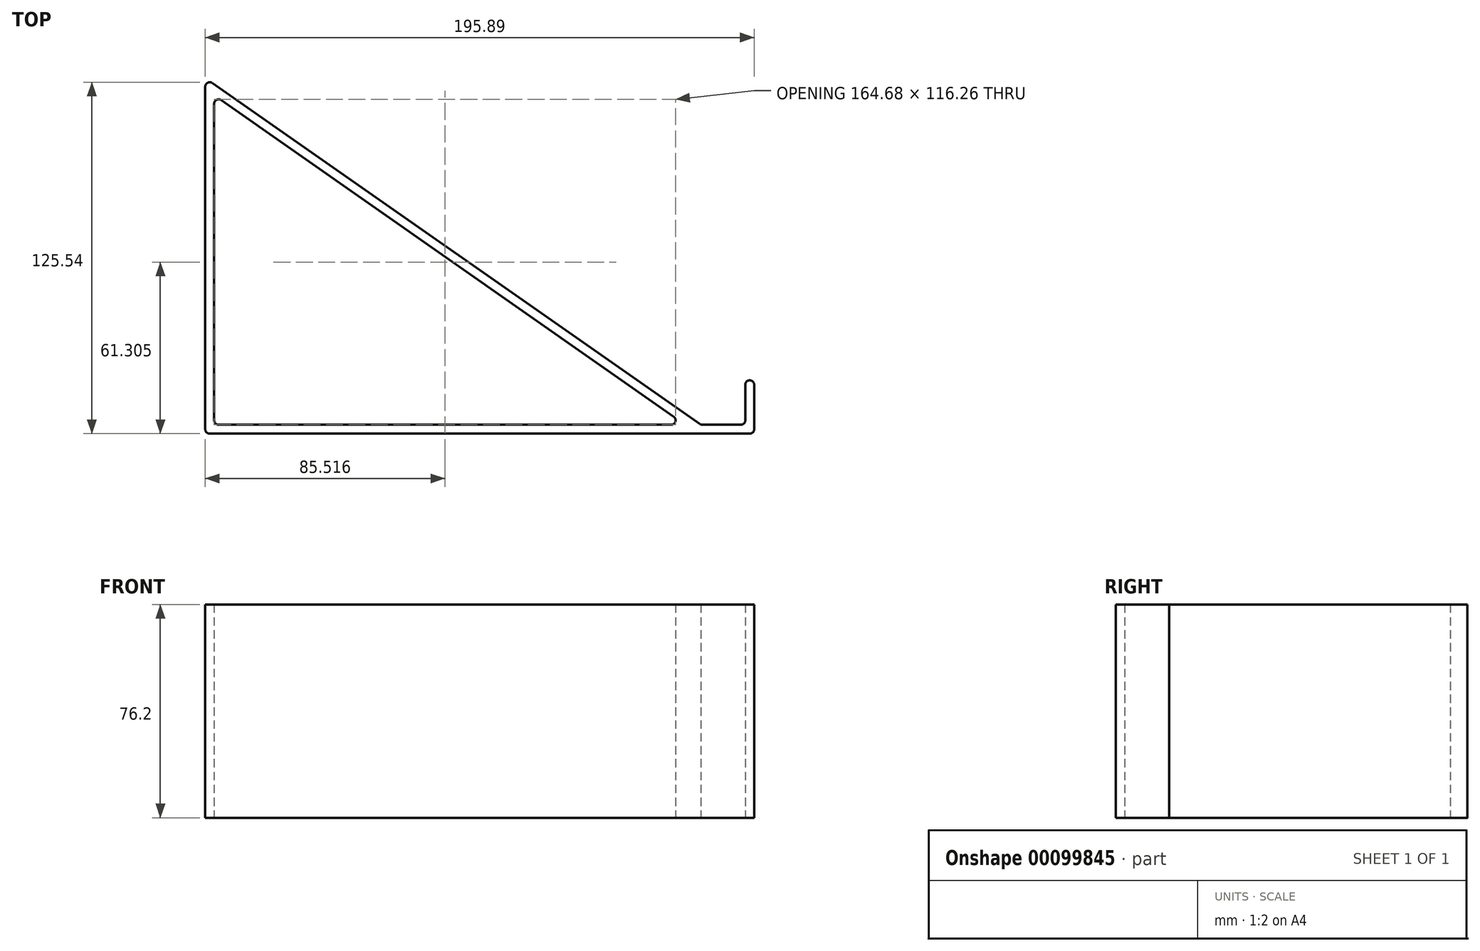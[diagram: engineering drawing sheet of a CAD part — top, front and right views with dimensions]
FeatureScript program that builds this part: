
annotation { "Feature Type Name" : "Feature", "Feature Type Description" : "" }
export const myFeature = defineFeature(function(context is Context, id is Id, definition is map)
    precondition{}
    {
        {
            var Q0;
            Q0=qCreatedBy(makeId("Top.planeOp"),FACE);
            var sketch = newSketch(context, id + "F0", { "sketchPlane" : qUnion([Q0])});
            skLineSegment(sketch, "E0", {"start": v(0, 1.59) * mm, "end": v(0, 123.95) * mm});
            skLineSegment(sketch, "E1", {"start": v(1.59, 0) * mm, "end": v(181.37, 0) * mm});
            skLineSegment(sketch, "E2", {"start": v(176.84, 3.18) * mm, "end": v(2.5, 125.25) * mm});
            skLineSegment(sketch, "E3", {"start": v(181.37, 0) * mm, "end": v(194.3, 0) * mm});
            skLineSegment(sketch, "E4", {"start": v(195.9, 1.59) * mm, "end": v(195.9, 17.46) * mm});
            skLineSegment(sketch, "E5", {"start": v(194.3, 19.05) * mm, "end": v(194.3, 19.05) * mm});
            skLineSegment(sketch, "E6", {"start": v(192.72, 17.46) * mm, "end": v(192.72, 4.76) * mm});
            skLineSegment(sketch, "E7", {"start": v(191.13, 3.18) * mm, "end": v(176.84, 3.18) * mm});
            skLineSegment(sketch, "E8.0", {"start": v(167.18, 6.06) * mm, "end": v(5.67, 119.15) * mm});
            skLineSegment(sketch, "E8.1", {"start": v(4.76, 3.18) * mm, "end": v(166.27, 3.18) * mm});
            skLineSegment(sketch, "E8.2", {"start": v(3.18, 4.76) * mm, "end": v(3.17, 117.85) * mm});
            skPoint(sketch, "E9.visualSharp", {"position": v(0, 127) * mm});
            skArc(sketch, "E9.filletArc", {"start": v(2.5, 125.25) * mm, "mid": v(0.85, 125.36) * mm, "end": v(0, 123.95) * mm});
            skPoint(sketch, "E10.visualSharp", {"position": v(3.17, 120.9) * mm});
            skArc(sketch, "E10.filletArc", {"start": v(5.67, 119.15) * mm, "mid": v(4.03, 119.26) * mm, "end": v(3.17, 117.85) * mm});
            skPoint(sketch, "E11.visualSharp", {"position": v(0, 0) * mm});
            skArc(sketch, "E11.filletArc", {"start": v(0, 1.59) * mm, "mid": v(0.46, 0.46) * mm, "end": v(1.59, 0) * mm});
            skPoint(sketch, "E12.visualSharp", {"position": v(3.18, 3.18) * mm});
            skArc(sketch, "E12.filletArc", {"start": v(3.18, 4.76) * mm, "mid": v(3.64, 3.64) * mm, "end": v(4.76, 3.18) * mm});
            skPoint(sketch, "E13.visualSharp", {"position": v(171.3, 3.18) * mm});
            skArc(sketch, "E13.filletArc", {"start": v(166.27, 3.17) * mm, "mid": v(167.78, 4.29) * mm, "end": v(167.18, 6.06) * mm});
            skPoint(sketch, "E14.visualSharp", {"position": v(195.9, 0) * mm});
            skArc(sketch, "E14.filletArc", {"start": v(194.3, 0) * mm, "mid": v(195.43, 0.46) * mm, "end": v(195.9, 1.59) * mm});
            skPoint(sketch, "E15.visualSharp", {"position": v(192.72, 3.18) * mm});
            skArc(sketch, "E15.filletArc", {"start": v(191.13, 3.18) * mm, "mid": v(192.25, 3.64) * mm, "end": v(192.72, 4.76) * mm});
            skPoint(sketch, "E16.visualSharp", {"position": v(192.72, 19.05) * mm});
            skArc(sketch, "E16.filletArc", {"start": v(194.3, 19.05) * mm, "mid": v(193.18, 18.59) * mm, "end": v(192.72, 17.46) * mm});
            skPoint(sketch, "E17.visualSharp", {"position": v(195.9, 19.05) * mm});
            skArc(sketch, "E17.filletArc", {"start": v(195.9, 17.46) * mm, "mid": v(195.43, 18.59) * mm, "end": v(194.3, 19.05) * mm});
            skSolve(sketch);
        }
        {
            var Q0;
            Q0 = qSketchRegion(id + "F0", true);
            extrude(context, id + "F1", {"entities" : qUnion([Q0]), "depth" : 76.2 * mm});
        }
    });
